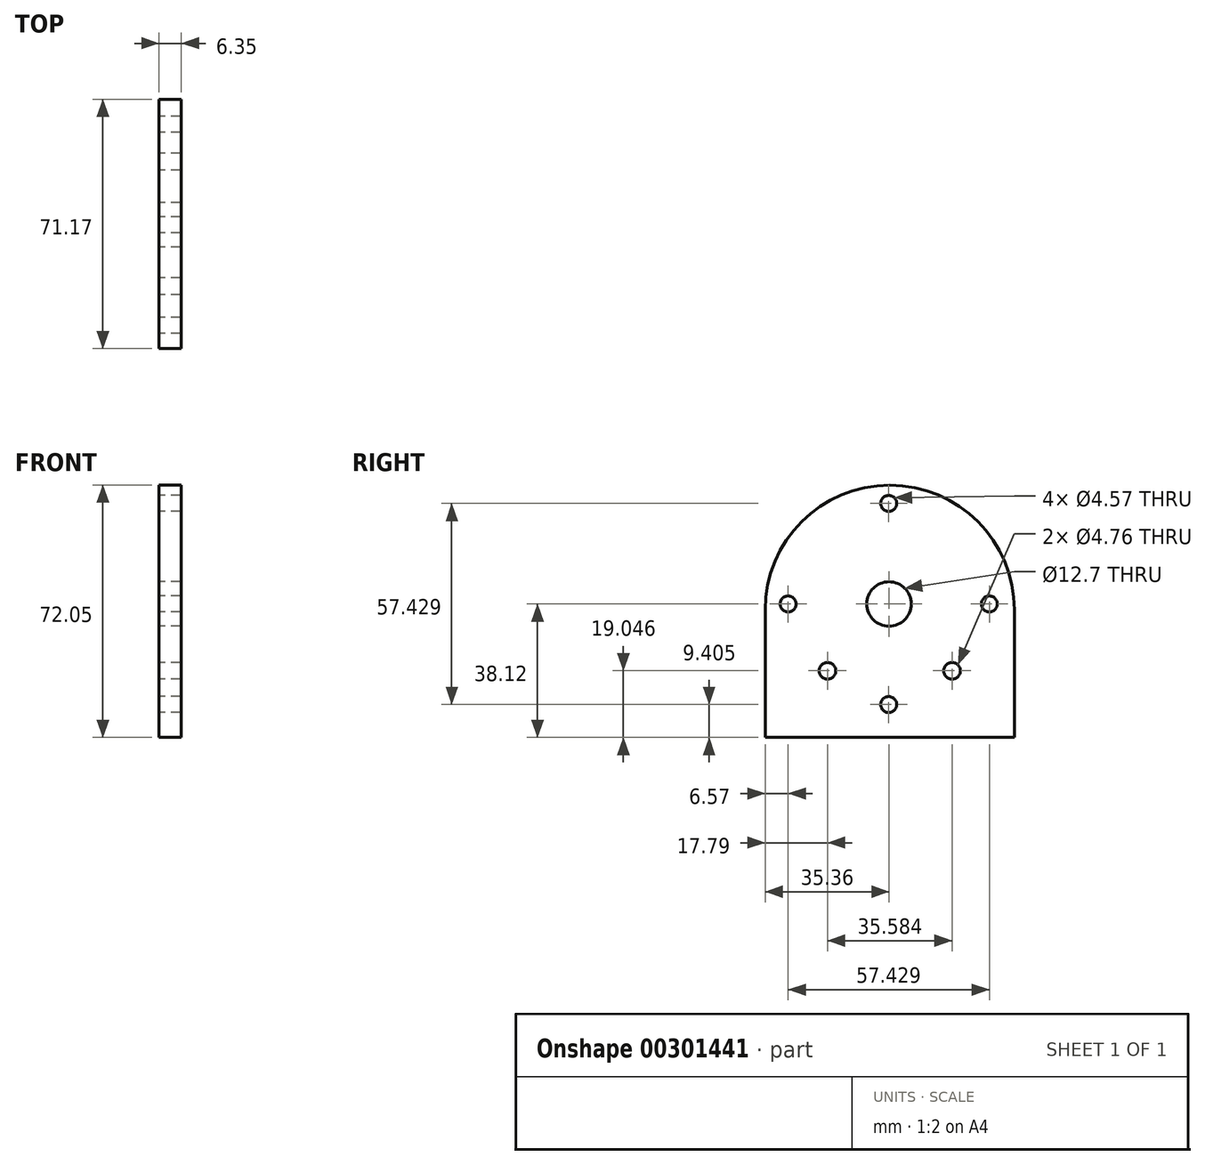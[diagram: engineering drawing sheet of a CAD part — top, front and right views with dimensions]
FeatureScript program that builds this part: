
annotation { "Feature Type Name" : "Feature", "Feature Type Description" : "" }
export const myFeature = defineFeature(function(context is Context, id is Id, definition is map)
    precondition{}
    {
        {
            var Q0;
            Q0=qCreatedBy(makeId("Right.planeOp"),FACE);
            var sketch = newSketch(context, id + "F0", { "sketchPlane" : qUnion([Q0])});
            skCircle(sketch, "E0", {"center": v(-0.07, 28.71) * mm, "radius": 2.29 * mm});
            skCircle(sketch, "E1.MirrorC", {"center": v(28.64, 0) * mm, "radius": 2.29 * mm});
            skCircle(sketch, "E2.MirrorC", {"center": v(-28.79, 0) * mm, "radius": 2.29 * mm});
            skCircle(sketch, "E3.MirrorC", {"center": v(-0.07, -28.71) * mm, "radius": 2.29 * mm});
            skLineSegment(sketch, "E4.1", {"start": v(28.64, 0) * mm, "end": v(28.64, 0) * mm});
            skLineSegment(sketch, "E5.bottom", {"start": v(-35.36, -38.12) * mm, "end": v(35.8, -38.12) * mm});
            skLineSegment(sketch, "E5.top", {"start": v(0, 33.93) * mm, "end": v(0.22, 33.93) * mm});
            skLineSegment(sketch, "E5.left", {"start": v(-35.36, -38.12) * mm, "end": v(-35.36, -1.65) * mm});
            skLineSegment(sketch, "E5.right", {"start": v(35.8, -38.12) * mm, "end": v(35.8, -1.65) * mm});
            skLineSegment(sketch, "E6", {"start": v(-35.36, -38.12) * mm, "end": v(0.22, -38.12) * mm});
            skLineSegment(sketch, "E7", {"start": v(0.22, -38.12) * mm, "end": v(-17.57, -38.12) * mm});
            skLineSegment(sketch, "E8", {"start": v(0.22, -38.12) * mm, "end": v(35.8, -38.12) * mm});
            skLineSegment(sketch, "E9", {"start": v(35.8, -38.12) * mm, "end": v(18.01, -38.12) * mm});
            skLineSegment(sketch, "E10", {"start": v(-17.57, -38.12) * mm, "end": v(-17.57, -19.07) * mm});
            skLineSegment(sketch, "E11", {"start": v(18.01, -38.12) * mm, "end": v(18.01, -19.07) * mm});
            skCircle(sketch, "E12", {"center": v(0, 0) * mm, "radius": 6.35 * mm});
            skCircle(sketch, "E13", {"center": v(-17.57, -19.07) * mm, "radius": 2.38 * mm});
            skCircle(sketch, "E14", {"center": v(18.01, -19.07) * mm, "radius": 2.38 * mm});
            skPoint(sketch, "E15.visualSharp", {"position": v(-35.36, 33.93) * mm});
            skArc(sketch, "E15.filletArc", {"start": v(0.22, 33.93) * mm, "mid": v(-24.94, 23.5) * mm, "end": v(-35.36, -1.65) * mm});
            skPoint(sketch, "E16.visualSharp", {"position": v(35.8, 33.93) * mm});
            skArc(sketch, "E16.filletArc", {"start": v(35.8, -1.65) * mm, "mid": v(25.38, 23.5) * mm, "end": v(0.22, 33.93) * mm});
            skPoint(sketch, "E17.end.orphan", {"position": v(35.8, 0) * mm});
            skPoint(sketch, "E18.end.orphan", {"position": v(-35.36, 0) * mm});
            skSolve(sketch);
        }
        {
            var Q0;
            Q0=makeQuery(id+"F0.imprint","IMPRINT",FACE,{"disambiguationData":[TD([[makeQuery(id+"F0.imprint","IMPRINT",EDGE,{"derivedFrom":sQuery(id+"F0.wireOp",EDGE,"E0")}),-1.0]])]});
            extrude(context, id + "F1", {"entities" : qUnion([Q0]), "depth" : 6.35 * mm, "offsetDistance" : 25.4 * mm});
        }
    });
